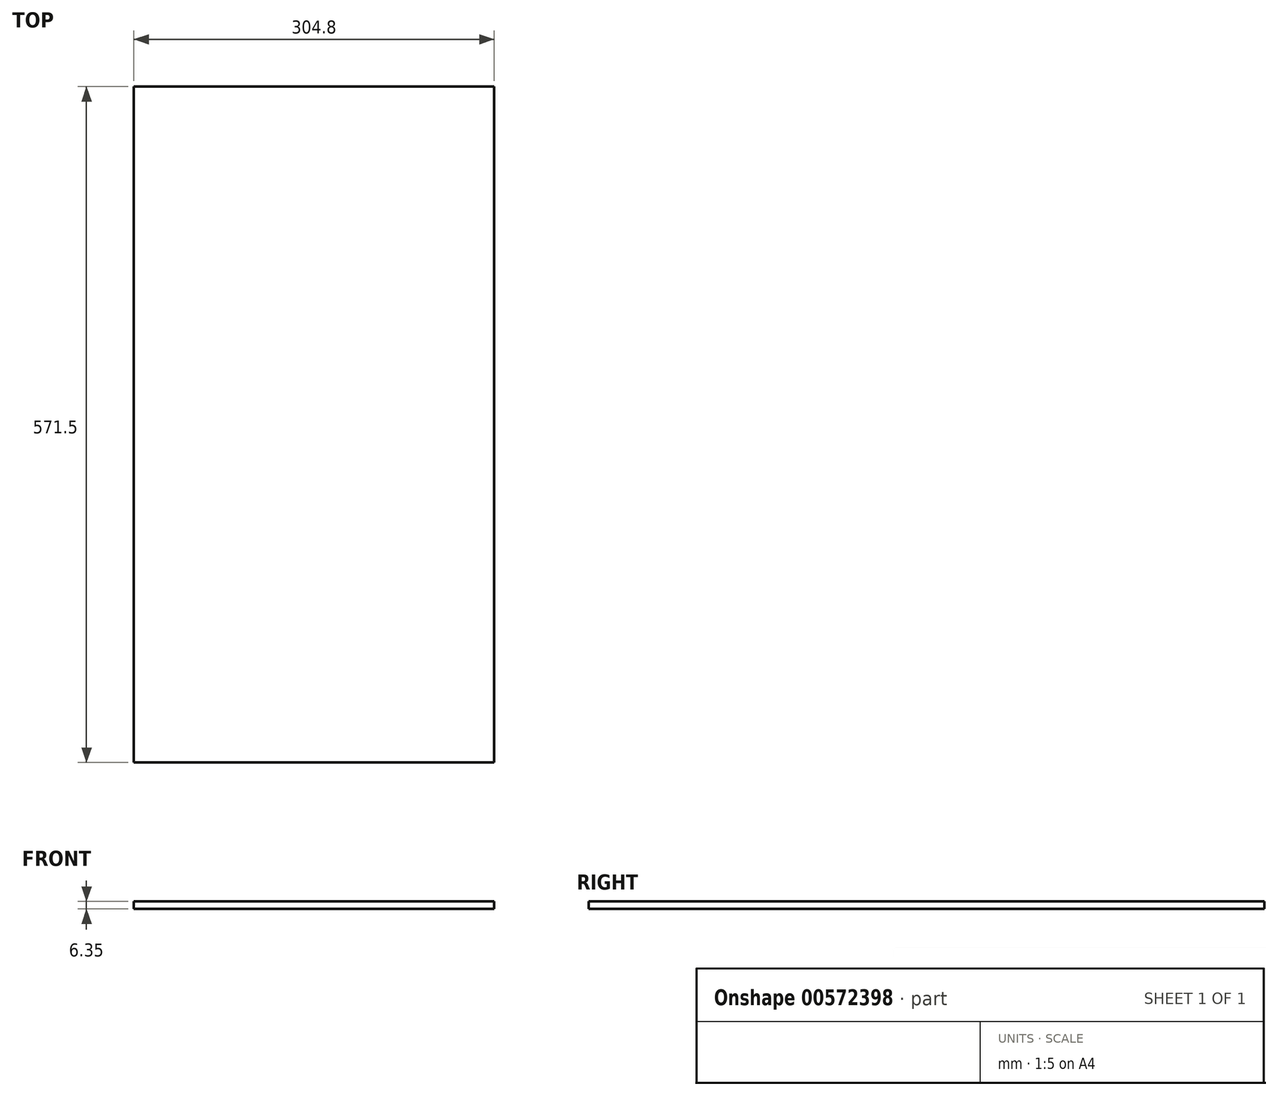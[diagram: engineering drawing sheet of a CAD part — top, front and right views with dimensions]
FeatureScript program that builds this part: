
annotation { "Feature Type Name" : "Feature", "Feature Type Description" : "" }
export const myFeature = defineFeature(function(context is Context, id is Id, definition is map)
    precondition{}
    {
        {
            var Q0;
            Q0=qCreatedBy(makeId("Top.planeOp"),FACE);
            var sketch = newSketch(context, id + "F0", { "sketchPlane" : qUnion([Q0])});
            skLineSegment(sketch, "E0.bottom", {"start": v(0, 0) * mm, "end": v(-304.8, 0) * mm});
            skLineSegment(sketch, "E0.top", {"start": v(0, 571.5) * mm, "end": v(-304.8, 571.5) * mm});
            skLineSegment(sketch, "E0.left", {"start": v(0, 0) * mm, "end": v(0, 571.5) * mm});
            skLineSegment(sketch, "E0.right", {"start": v(-304.8, 0) * mm, "end": v(-304.8, 571.5) * mm});
            skSolve(sketch);
        }
        {
            var Q0;
            Q0 = qSketchRegion(id + "F0", true);
            extrude(context, id + "F1", {"entities" : qUnion([Q0]), "depth" : 6.35 * mm, "offsetDistance" : 25.4 * mm});
        }
    });
